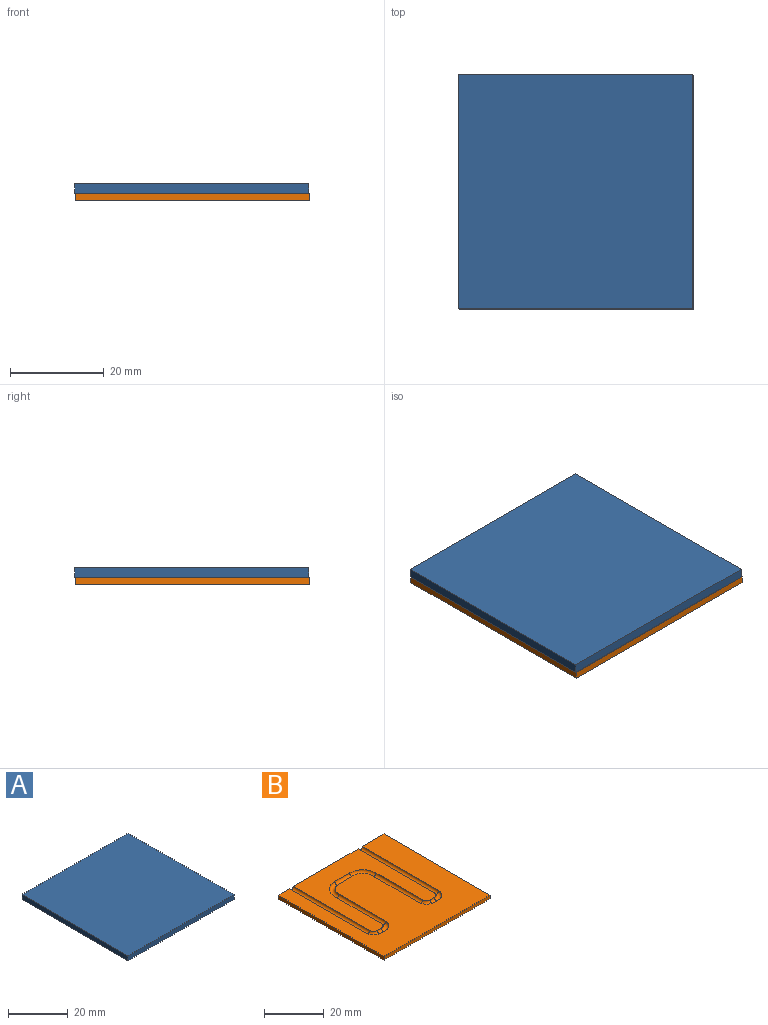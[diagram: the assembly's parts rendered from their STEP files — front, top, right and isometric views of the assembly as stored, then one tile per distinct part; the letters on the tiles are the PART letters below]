
ASSEMBLY  parts=2 mates=1
PART A: 6 faces, bbox 50x50x2 mm
  f0: plane 50x2mm, normal (-1,0,0), area 100mm2, adj f1,f3,f4,f5
  f1: plane 50x2mm, normal (0,-1,0), area 100mm2, adj f0,f2,f4,f5
  f2: plane 50x2mm, normal (1,0,0), area 100mm2, adj f1,f3,f4,f5
  f3: plane 50x2mm, normal (0,1,0), area 100mm2, adj f0,f2,f4,f5
  f4: plane 50x50mm, normal (0,0,1), area 2500mm2, adj f0,f1,f2,f3
  f5: plane 50x50mm, normal (0,0,-1), area 2500mm2, adj f0,f1,f2,f3
PART B: 20 faces, bbox 50x50x2.2 mm
  f0: plane 50x1.5mm, normal (0,1,0), area 71.9mm2, adj f1,f2,f3,f5,f6,f7,f19
  f1: plane 50x50mm, normal (0,0,1), area 1592.8mm2, adj f0,f2,f3,f4,f7,f8,f9,f10
  f2: plane 50x1.5mm, normal (1,0,0), area 75mm2, adj f0,f1,f4,f6
  f3: plane 50x1.5mm, normal (-1,0,0), area 75mm2, adj f0,f1,f4,f6
  f4: plane 50x1.5mm, normal (0,-1,0), area 75mm2, adj f1,f2,f3,f6
  f5: plane 37.78x30.56mm, normal (0,0,1), area 585.5mm2, adj f0,f7,f8,f9,f10,f11,f12,f13
  f6: plane 50x50mm, normal (0,0,-1), area 2500mm2, adj f0,f2,f3,f4
  f7: cylinder r=1mm len=36mm, axis (0,-1,0), area 113.1mm2, adj f0,f1,f5,f8
  f8: torus R=2.78mm, axis (0,0,1), area 13.7mm2, adj f1,f5,f7,f9
  f9: cylinder r=1mm len=2mm, axis (1,0,0), area 6.3mm2, adj f1,f5,f8,f10
  f10: torus R=2.78mm, axis (0,0,1), area 13.7mm2, adj f1,f5,f9,f11
  f11: cylinder r=1mm len=22mm, axis (0,1,0), area 69.1mm2, adj f1,f5,f10,f12
  f12: torus R=5.22mm, axis (0,0,-1), area 25.8mm2, adj f1,f5,f11,f13
  f13: cylinder r=1mm len=7mm, axis (1,0,0), area 22mm2, adj f1,f5,f12,f14
  f14: torus R=5.22mm, axis (0,0,-1), area 25.8mm2, adj f1,f5,f13,f15
  f15: cylinder r=1mm len=22mm, axis (0,-1,0), area 69.1mm2, adj f1,f5,f14,f16
  f16: torus R=2.78mm, axis (0,0,1), area 13.7mm2, adj f1,f5,f15,f17
  f17: cylinder r=1mm len=2mm, axis (1,0,0), area 6.3mm2, adj f1,f5,f16,f18
  f18: torus R=2.78mm, axis (0,0,1), area 13.7mm2, adj f1,f5,f17,f19
  f19: cylinder r=1mm len=36mm, axis (0,1,0), area 113.1mm2, adj f0,f1,f5,f18
PLACE A rot(axis=(1,0,0),180deg) t=(16.57,-34.18,12)mm
PLACE B t=(16.71,15.67,8.5)mm
MATE planar B.f1 <-> A.f4  axis (0,0,1) through (-28.08,-20.33,10)mm
